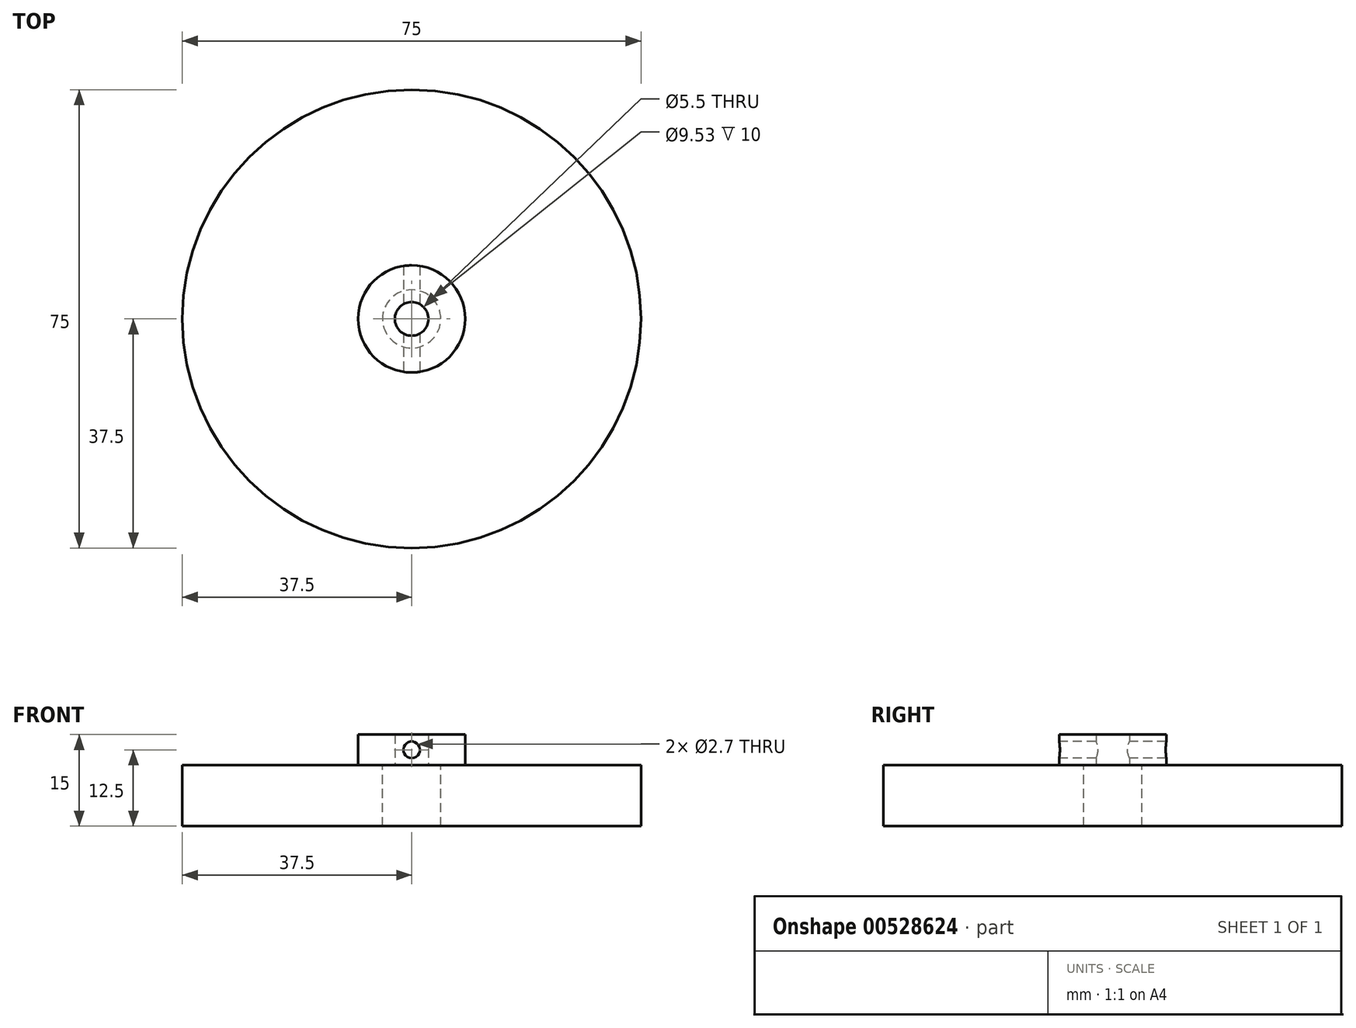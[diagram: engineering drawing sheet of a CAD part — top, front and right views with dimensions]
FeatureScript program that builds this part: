
annotation { "Feature Type Name" : "Feature", "Feature Type Description" : "" }
export const myFeature = defineFeature(function(context is Context, id is Id, definition is map)
    precondition{}
    {
        {
            var Q0;
            Q0=qCreatedBy(makeId("Top.planeOp"),FACE);
            var sketch = newSketch(context, id + "F0", { "sketchPlane" : qUnion([Q0])});
            skCircle(sketch, "E0", {"center": v(0, 0) * mm, "radius": 2.75 * mm});
            skCircle(sketch, "E1", {"center": v(0, 0) * mm, "radius": 37.5 * mm});
            skSolve(sketch);
        }
        {
            var Q0;
            Q0=makeQuery(id+"F0.imprint","IMPRINT",FACE,{"disambiguationData":[TD([[makeQuery(id+"F0.imprint","IMPRINT",EDGE,{"derivedFrom":sQuery(id+"F0.wireOp",EDGE,"E0")}),-1.0]])]});
            extrude(context, id + "F1", {"entities" : qUnion([Q0]), "depth" : 10 * mm, "offsetDistance" : 25 * mm});
        }
        {
            var Q0;
            Q0=makeQuery(id+"F1.opExtrude","CAP_FACE",FACE,{"disambiguationData":[OSD([sQuery(id+"F0.wireOp",EDGE,"E0"),sQuery(id+"F0.wireOp",EDGE,"E1")])],"isStart":false});
            var sketch = newSketch(context, id + "F2", { "sketchPlane" : qUnion([Q0])});
            skCircle(sketch, "E2", {"center": v(0, 0) * mm, "radius": 6.75 * mm});
            skSolve(sketch);
        }
        {
            var Q0;
            Q0=makeQuery(id+"F2.imprint","IMPRINT",FACE,{"disambiguationData":[TD([[makeQuery(id+"F2.imprint","IMPRINT",EDGE,{"derivedFrom":sQuery(id+"F2.wireOp",EDGE,"E2")}),1.0]])]});
            extrude(context, id + "F3", {"entities" : qUnion([Q0]), "operationType" : NewBodyOperationType.ADD, "depth" : 5 * mm, "offsetDistance" : 25 * mm});
        }
        {
            var Q0;
            Q0=qCreatedBy(makeId("Front.planeOp"),FACE);
            var sketch = newSketch(context, id + "F4", { "sketchPlane" : qUnion([Q0])});
            skLineSegment(sketch, "E3.0", {"start": v(-6.75, 15) * mm, "end": v(6.75, 15) * mm});
            skLineSegment(sketch, "E4.0", {"start": v(-37.5, 10) * mm, "end": v(37.5, 10) * mm});
            skLineSegment(sketch, "E5", {"start": v(6.75, 15) * mm, "end": v(6.75, 10) * mm});
            skLineSegment(sketch, "E6", {"start": v(-6.75, 15) * mm, "end": v(-6.75, 10) * mm});
            skCircle(sketch, "E7", {"center": v(0, 12.5) * mm, "radius": 1.35 * mm});
            skPoint(sketch, "E7.centerSnap0", {"position": v(0, 15) * mm});
            skPoint(sketch, "E7.centerSnap1", {"position": v(6.75, 12.5) * mm});
            skSolve(sketch);
        }
        {
            var Q0;
            Q0=makeQuery(id+"F4.imprint","IMPRINT",FACE,{"disambiguationData":[TD([[makeQuery(id+"F4.imprint","IMPRINT",EDGE,{"derivedFrom":sQuery(id+"F4.wireOp",EDGE,"E7")}),1.0]])]});
            extrude(context, id + "F5", {"entities" : qUnion([Q0]), "operationType" : NewBodyOperationType.REMOVE, "oppositeDirection" : true, "depth" : 25 * mm, "offsetDistance" : 25 * mm, "hasSecondDirection" : true, "secondDirectionOppositeDirection" : false, "secondDirectionDepth" : 25 * mm});
        }
        {
            var Q0;
            Q0=makeQuery(id+"F0.imprint","IMPRINT",FACE,{"disambiguationData":[TD([[makeQuery(id+"F0.imprint","IMPRINT",EDGE,{"derivedFrom":sQuery(id+"F0.wireOp",EDGE,"E0")}),-1.0]])]});
            extrude(context, id + "F6", {"entities" : qUnion([Q0]), "depth" : 10 * mm, "offsetDistance" : 25 * mm});
        }
        {
            var Q0;
            Q0=makeQuery(id+"F6.opExtrude","CAP_FACE",FACE,{"disambiguationData":[OSD([sQuery(id+"F0.wireOp",EDGE,"E0"),sQuery(id+"F0.wireOp",EDGE,"E1")])],"isStart":false});
            var sketch = newSketch(context, id + "F7", { "sketchPlane" : qUnion([Q0])});
            skCircle(sketch, "E8", {"center": v(0, 0) * mm, "radius": 4.76 * mm});
            skSolve(sketch);
        }
        {
            var Q0;
            Q0=makeQuery(id+"F7.imprint","IMPRINT",FACE,{"disambiguationData":[TD([[makeQuery(id+"F7.imprint","IMPRINT",EDGE,{"derivedFrom":sQuery(id+"F7.wireOp",EDGE,"E8")}),1.0]])]});
            extrude(context, id + "F8", {"entities" : qUnion([Q0]), "operationType" : NewBodyOperationType.REMOVE, "oppositeDirection" : true, "depth" : 25 * mm, "offsetDistance" : 25 * mm});
        }
        {
            var Q0;
            Q0=makeQuery(id+"F6.opExtrude","CAP_FACE",FACE,{"disambiguationData":[OSD([sQuery(id+"F0.wireOp",EDGE,"E0"),sQuery(id+"F0.wireOp",EDGE,"E1")])],"isStart":false});
            var sketch = newSketch(context, id + "F9", { "sketchPlane" : qUnion([Q0])});
            skCircle(sketch, "E9", {"center": v(0, 0) * mm, "radius": 8.76 * mm});
            skSolve(sketch);
        }
        {
            var Q0;
            Q0=makeQuery(id+"F9.imprint","IMPRINT",FACE,{"disambiguationData":[TD([[makeQuery(id+"F9.imprint","IMPRINT",EDGE,{"derivedFrom":sQuery(id+"F9.wireOp",EDGE,"E9")}),1.0]])]});
            extrude(context, id + "F10", {"entities" : qUnion([Q0]), "operationType" : NewBodyOperationType.ADD, "depth" : 5 * mm, "offsetDistance" : 25 * mm});
        }
        {
            var Q0;
            Q0=makeQuery(id+"F4.imprint","IMPRINT",FACE,{"disambiguationData":[TD([[makeQuery(id+"F4.imprint","IMPRINT",EDGE,{"derivedFrom":sQuery(id+"F4.wireOp",EDGE,"E7")}),1.0]])]});
            extrude(context, id + "F11", {"entities" : qUnion([Q0]), "operationType" : NewBodyOperationType.REMOVE, "oppositeDirection" : true, "depth" : 25 * mm, "offsetDistance" : 25 * mm, "hasSecondDirection" : true, "secondDirectionOppositeDirection" : false, "secondDirectionDepth" : 25 * mm});
        }
    });
